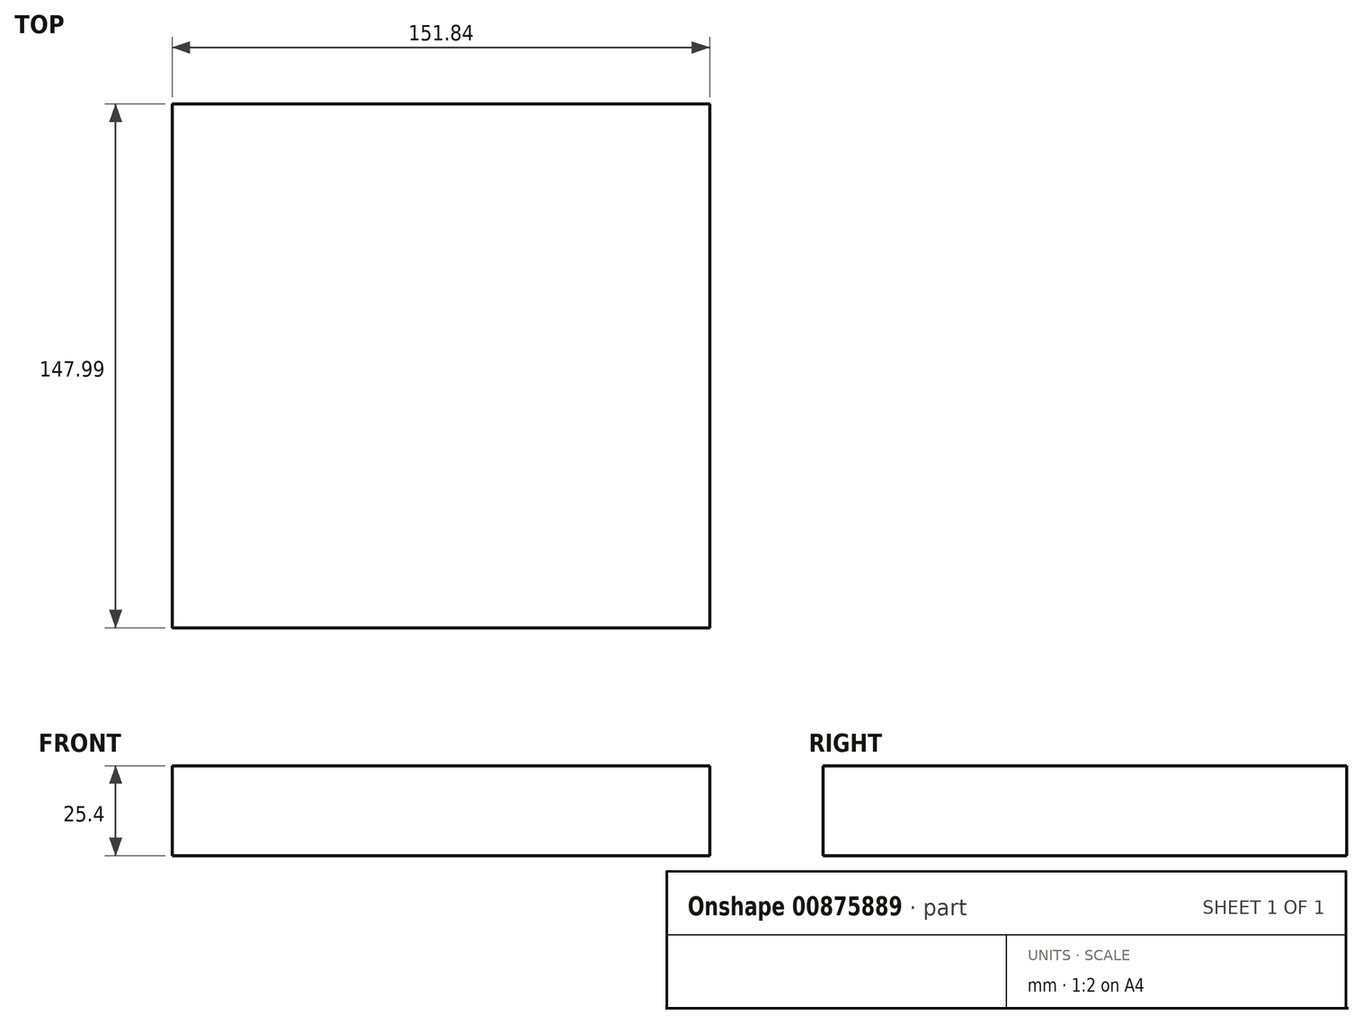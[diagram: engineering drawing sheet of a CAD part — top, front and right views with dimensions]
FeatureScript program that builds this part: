
annotation { "Feature Type Name" : "Feature", "Feature Type Description" : "" }
export const myFeature = defineFeature(function(context is Context, id is Id, definition is map)
    precondition{}
    {
        {
            var Q0;
            Q0=qCreatedBy(makeId("Top.planeOp"),FACE);
            var sketch = newSketch(context, id + "F0", { "sketchPlane" : qUnion([Q0])});
            skLineSegment(sketch, "E0.bottom", {"start": v(-75.92, 77.34) * mm, "end": v(75.92, 77.34) * mm});
            skLineSegment(sketch, "E0.top", {"start": v(-75.92, -70.65) * mm, "end": v(75.92, -70.65) * mm});
            skLineSegment(sketch, "E0.left", {"start": v(-75.92, 77.34) * mm, "end": v(-75.92, -70.65) * mm});
            skLineSegment(sketch, "E0.right", {"start": v(75.92, 77.34) * mm, "end": v(75.92, -70.65) * mm});
            skPoint(sketch, "E0.middle", {"position": v(0, 3.35) * mm});
            skSolve(sketch);
        }
        {
            var Q0;
            Q0=makeQuery(id+"F0.imprint","IMPRINT",FACE,{"disambiguationData":[TD([[makeQuery(id+"F0.imprint","IMPRINT",EDGE,{"derivedFrom":sQuery(id+"F0.wireOp",EDGE,"E0.bottom")}),-1.0]])]});
            extrude(context, id + "F1", {"entities" : qUnion([Q0]), "depth" : 25.4 * mm, "offsetDistance" : 25.4 * mm});
        }
    });
